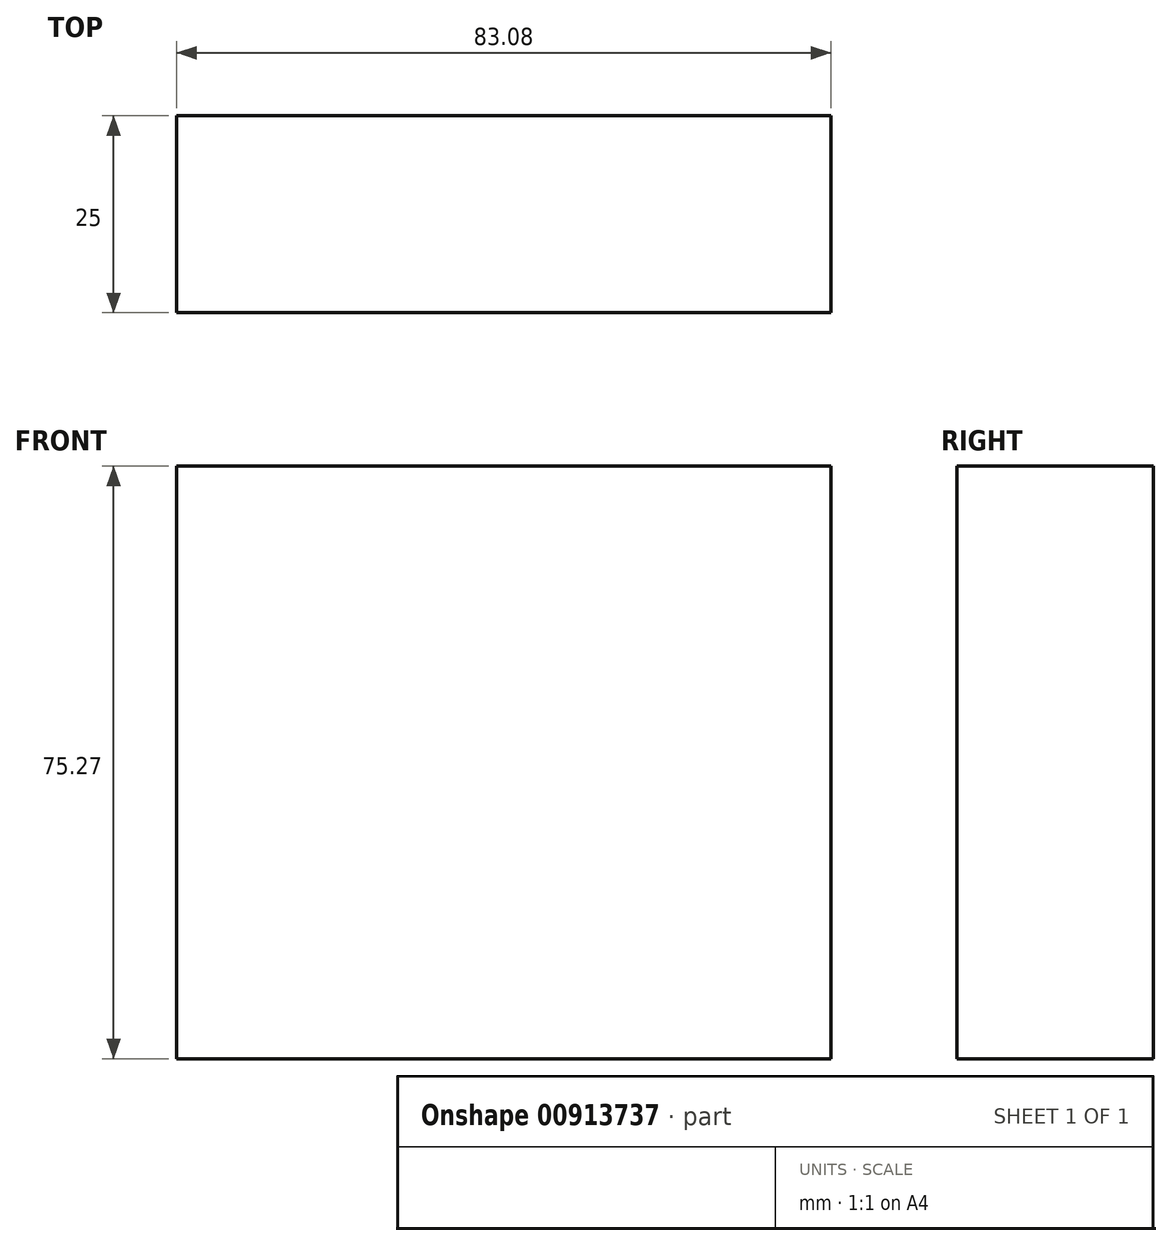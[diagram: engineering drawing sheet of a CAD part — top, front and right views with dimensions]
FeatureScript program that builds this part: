
annotation { "Feature Type Name" : "Feature", "Feature Type Description" : "" }
export const myFeature = defineFeature(function(context is Context, id is Id, definition is map)
    precondition{}
    {
        {
            var Q0;
            Q0=qCreatedBy(makeId("Front.planeOp"),FACE);
            var sketch = newSketch(context, id + "F0", { "sketchPlane" : qUnion([Q0])});
            skLineSegment(sketch, "E0.bottom", {"start": v(-131.28, -27.03) * mm, "end": v(-48.2, -27.03) * mm});
            skLineSegment(sketch, "E0.top", {"start": v(-131.28, 48.24) * mm, "end": v(-48.2, 48.24) * mm});
            skLineSegment(sketch, "E0.left", {"start": v(-131.28, -27.03) * mm, "end": v(-131.28, 48.24) * mm});
            skLineSegment(sketch, "E0.right", {"start": v(-48.2, -27.03) * mm, "end": v(-48.2, 48.24) * mm});
            skPoint(sketch, "E0.middle", {"position": v(-89.74, 10.6) * mm});
            skSolve(sketch);
        }
        {
            var Q0;
            Q0=makeQuery(id+"F0.imprint","IMPRINT",FACE,{"disambiguationData":[TD([[makeQuery(id+"F0.imprint","IMPRINT",EDGE,{"derivedFrom":sQuery(id+"F0.wireOp",EDGE,"E0.bottom")}),1.0]])]});
            extrude(context, id + "F1", {"entities" : qUnion([Q0]), "depth" : 25 * mm, "offsetDistance" : 25 * mm});
        }
    });
